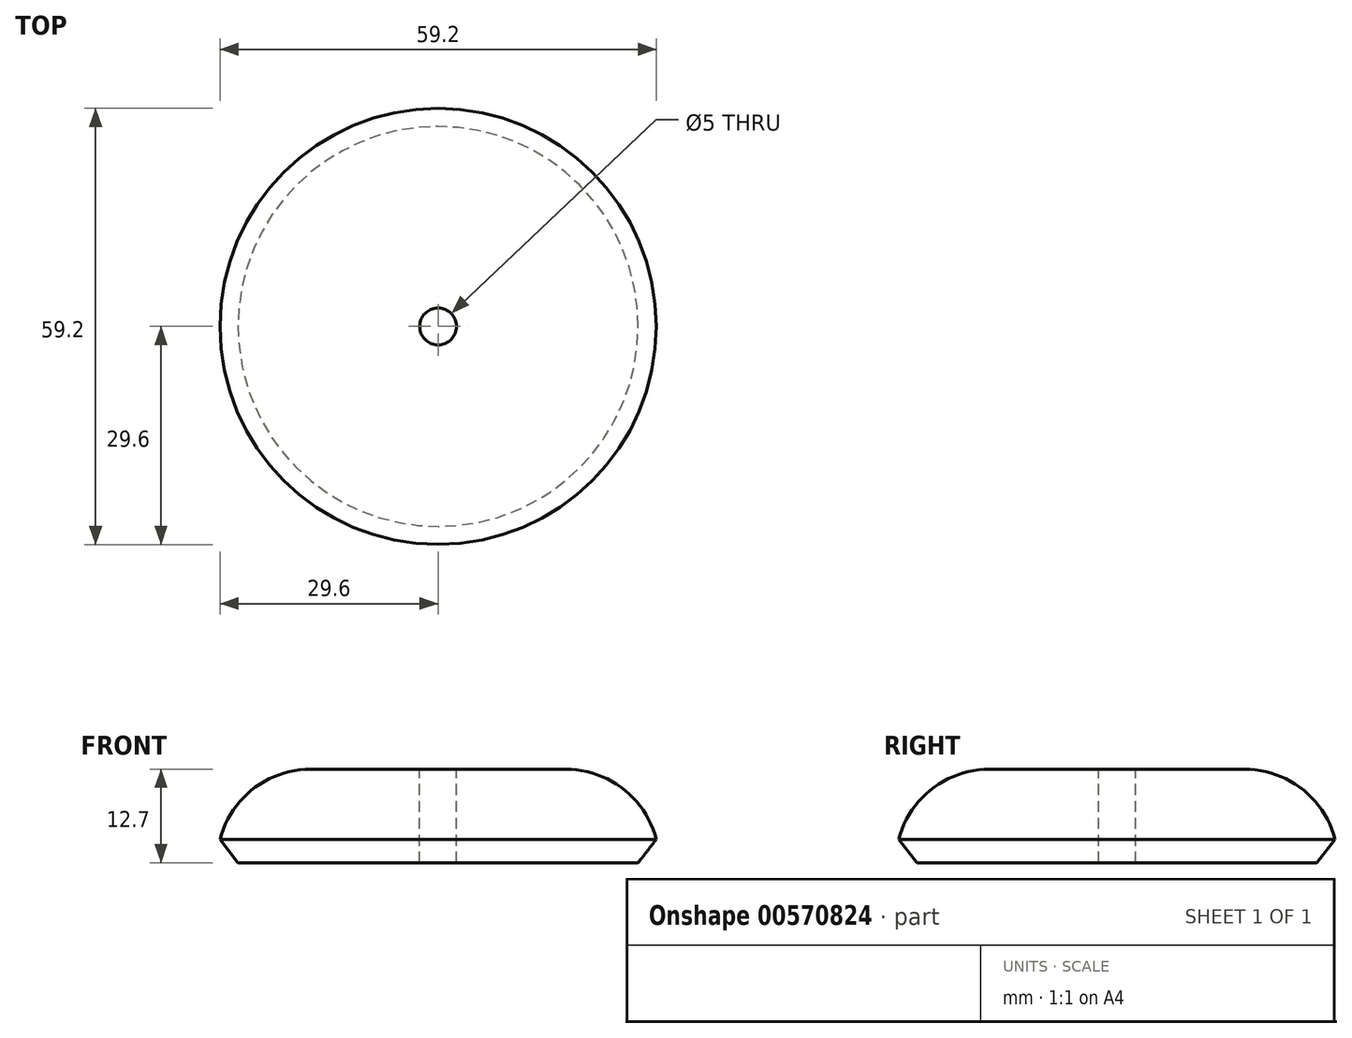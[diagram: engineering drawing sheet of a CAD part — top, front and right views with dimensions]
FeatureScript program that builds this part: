
annotation { "Feature Type Name" : "Feature", "Feature Type Description" : "" }
export const myFeature = defineFeature(function(context is Context, id is Id, definition is map)
    precondition{}
    {
        {
            var Q0;
            Q0=qCreatedBy(makeId("Top.planeOp"),FACE);
            var sketch = newSketch(context, id + "F0", { "sketchPlane" : qUnion([Q0])});
            skCircle(sketch, "E0", {"center": v(0, 0) * mm, "radius": 30 * mm});
            skSolve(sketch);
        }
        {
            var Q0;
            Q0=makeQuery(id+"F0.imprint","IMPRINT",FACE,{"disambiguationData":[TD([[makeQuery(id+"F0.imprint","IMPRINT",EDGE,{"derivedFrom":sQuery(id+"F0.wireOp",EDGE,"E0")}),1.0]])]});
            extrude(context, id + "F1", {"entities" : qUnion([Q0]), "depth" : 12.7 * mm, "offsetDistance" : 25.4 * mm});
        }
        {
            var Q0;
            Q0=makeQuery(id+"F1.opExtrude","CAP_EDGE",EDGE,{"disambiguationData":[OSD([sQuery(id+"F0.wireOp",EDGE,"E0")])],"isStart":false});
            fillet(context, id + "F2", {"entities" : qUnion([Q0]), "radius" : 12.7 * mm, "tangentPropagation" : true, "allowEdgeOverflow" : false});
        }
        {
            var Q0;
            {var subQ0=sQuery(id+"F0.wireOp",EDGE,"E0");Q0=makeQuery(id+"F2.opFillet","BLEND_EDGE",EDGE,{"blendedFrom":[makeQuery(id+"F1.opExtrude","CAP_EDGE",EDGE,{"disambiguationData":[OSD([subQ0])],"isStart":false}),makeQuery(id+"F1.opExtrude","CAP_FACE",FACE,{"disambiguationData":[OSD([subQ0])],"isStart":true})],"blendedInto":[makeQuery(id+"F1.opExtrude","CAP_FACE",FACE,{"disambiguationData":[OSD([subQ0])],"isStart":true})]});}
            chamfer(context, id + "F3", {"entities" : qUnion([Q0]), "width" : 2.54 * mm, "tangentPropagation" : true});
        }
        {
            var Q0;
            Q0=makeQuery(id+"F1.opExtrude","CAP_FACE",FACE,{"disambiguationData":[OSD([sQuery(id+"F0.wireOp",EDGE,"E0")])],"isStart":false});
            var sketch = newSketch(context, id + "F4", { "sketchPlane" : qUnion([Q0])});
            skPoint(sketch, "E1", {"position": v(0, 0) * mm});
            skSolve(sketch);
        }
        {
            var Q0;
            Q0=sQuery(id+"F4.wireOp",VERTEX,"E1");
            var Q1;
            Q1=makeQuery(id+"F1.opExtrude","SWEPT_BODY",BODY,{"disambiguationData":[OSD([sQuery(id+"F0.wireOp",EDGE,"E0")])]});
            hole(context, id + "F5", {"style" : HoleStyle.SIMPLE, "endStyle" : HoleEndStyle.THROUGH, "holeDiameter" : 5 * mm, "majorDiameter" : 6.35 * mm, "isTappedThrough" : true, "tappedDepth" : 12.7 * mm, "tapClearance" : 3, "locations" : qUnion([Q0]), "scope" : qUnion([Q1])});
        }
    });
